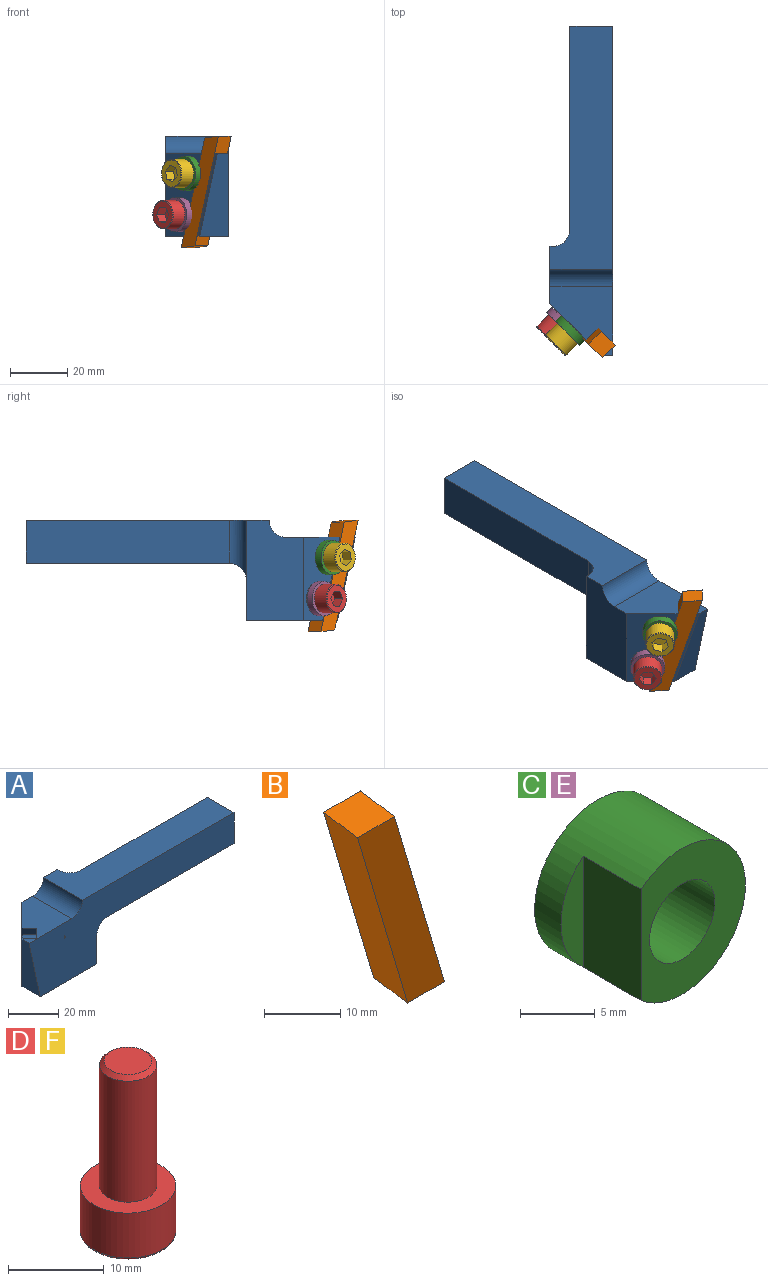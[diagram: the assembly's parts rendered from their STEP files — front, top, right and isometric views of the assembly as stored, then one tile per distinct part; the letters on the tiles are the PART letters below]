
ASSEMBLY  parts=6 mates=9
PART A: 26 faces, bbox 115x22.1x35 mm
  f0: plane 15x15mm, normal (1,0,0), area 225mm2, adj f4,f10,f22,f23
  f1: plane 4.64x4.64mm, normal (-0.68,-0.68,-0.29), area 13.6mm2, adj f7,f8,f15,f18
  f2: plane 5.8x5.4mm, normal (-0.68,-0.68,-0.29), area 35.7mm2, adj f8,f15,f17,f18
  f3: cylinder r=2.5mm len=11.38mm, axis (-0.71,0.71,0), area 174.3mm2, adj f4,f15,f16
  f4: plane 115.03x35.03mm, normal (0,-1,0), area 2230.9mm2, adj f0,f3,f6,f7,f10,f11,f12,f16
  f5: plane 29x6.77mm, normal (-0.71,0.71,0), area 25mm2, adj f6,f7,f12,f13
  f6: plane 24x22mm, normal (0,0,1), area 326.9mm2, adj f4,f5,f8,f9,f11,f12,f13,f14
  f7: plane 31.84x22mm, normal (0,0,-1), area 591.2mm2, adj f1,f4,f5,f8,f9,f12,f13,f15
  f8: plane 29x12.7mm, normal (-0.71,0.71,0), area 193.1mm2, adj f1,f2,f6,f7,f9,f14,f17,f18
  f9: plane 35x20mm, normal (0,1,0), area 635.7mm2, adj f6,f7,f8,f10,f11,f21
  f10: plane 85x22mm, normal (0,0,1), area 1338.7mm2, adj f0,f4,f9,f11,f21,f22,f24
  f11: cylinder r=6mm len=22mm, axis (0,1,0), area 207.3mm2, adj f4,f6,f9,f10
  f12: plane 29x10.16mm, normal (-0.98,0,-0.21), area 210mm2, adj f4,f5,f6,f7
  f13: plane 29x10.34mm, normal (0.68,0.68,0.29), area 178.7mm2, adj f5,f6,f7,f15
  f14: plane 4.99x4.99mm, normal (-0.68,-0.68,-0.29), area 23.8mm2, adj f6,f8,f15,f17
  f15: plane 29x16.43mm, normal (-0.71,0.71,0), area 354.4mm2, adj f1,f2,f3,f6,f7,f13,f14,f17
  f16: cone r=0mm half-angle=59deg, axis (-0.71,0.71,0), area 22.7mm2, adj f3,f4
  f17: cylinder r=6mm len=12.03mm, axis (-0.71,0.71,0), area 162.9mm2, adj f2,f8,f14,f15
  f18: cylinder r=6mm len=12.03mm, axis (-0.71,0.71,0), area 162.9mm2, adj f1,f2,f8,f15
  f19: cone r=0mm half-angle=59deg, axis (-0.71,0.71,0), area 22.9mm2, adj f20
  f20: cylinder r=2.5mm len=11.38mm, axis (-0.71,0.71,0), area 174.4mm2, adj f15,f19
  f21: plane 35x22mm, normal (1,0,0), area 329mm2, adj f4,f7,f9,f10,f24,f25
  f22: plane 71x15mm, normal (0,1,0), area 1065mm2, adj f0,f10,f23,f24
  f23: plane 71x15mm, normal (0,0,-1), area 1065mm2, adj f0,f4,f22,f25
  f24: cylinder r=6mm len=21mm, axis (0,0,1), area 161.9mm2, adj f10,f21,f22,f25
  f25: cylinder r=6mm len=21mm, axis (0,1,0), area 161.9mm2, adj f4,f21,f23,f24
PART B: 6 faces, bbox 21.7x11.8x37.7 mm
  f0: plane 37.68x14.84mm, normal (0.93,-0.06,0.37), area 254mm2, adj f1,f3,f4,f5
  f1: plane 6.84x6.28mm, normal (0,-0.15,0.99), area 43.4mm2, adj f0,f2,f4,f5
  f2: plane 37.68x14.84mm, normal (-0.93,0.06,-0.37), area 254mm2, adj f1,f3,f4,f5
  f3: plane 6.84x6.28mm, normal (0,0.15,-0.99), area 43.4mm2, adj f0,f2,f4,f5
  f4: plane 36.73x21.68mm, normal (0,-0.99,-0.15), area 254mm2, adj f0,f1,f2,f3
  f5: plane 36.73x21.68mm, normal (0,0.99,0.15), area 254mm2, adj f0,f1,f2,f3
PART C: 6 faces, bbox 12x8x12 mm
  f0: plane 12x9.9mm, normal (0,-1,0), area 69.6mm2, adj f1,f2,f4
  f1: cylinder r=3.1mm len=8mm, axis (0,1,0), area 155.8mm2, adj f0,f3
  f2: cylinder r=6mm len=12mm, axis (0,1,0), area 244.6mm2, adj f0,f3,f4,f5
  f3: plane 12x12mm, normal (0,1,0), area 82.9mm2, adj f1,f2
  f4: plane 9.12x5.5mm, normal (-1,0,0), area 50.2mm2, adj f0,f2,f5
  f5: plane 9.12x2.1mm, normal (0,-1,0), area 13.3mm2, adj f2,f4
PART D: 14 faces, bbox 10.8x10.8x22 mm
  f0: plane 10x10mm, normal (0,0,1), area 50.3mm2, adj f1,f3
  f1: cylinder r=5mm len=10mm, axis (0,0,-1), area 180.6mm2, adj f0,f12
  f2: plane 9.5x9.5mm, normal (0,0,-1), area 47.5mm2, adj f5,f6,f7,f8,f9,f10,f12
  f3: cylinder r=3mm len=15.5mm, axis (0,0,-1), area 292.2mm2, adj f0,f13
  f4: plane 5x5mm, normal (0,0,1), area 19.6mm2, adj f13
  f5: plane 4x2.6mm, normal (0.87,-0.5,0), area 12mm2, adj f2,f6,f10,f11
  f6: plane 4x2.6mm, normal (0.87,0.5,0), area 12mm2, adj f2,f5,f7,f11
  f7: plane 4x3mm, normal (0,1,0), area 12mm2, adj f2,f6,f8,f11
  f8: plane 4x2.6mm, normal (-0.87,0.5,0), area 12mm2, adj f2,f7,f9,f11
  f9: plane 4x2.6mm, normal (-0.87,-0.5,0), area 12mm2, adj f2,f8,f10,f11
  f10: plane 4x3mm, normal (0,-1,0), area 12mm2, adj f2,f5,f9,f11
  f11: plane 6x5.2mm, normal (0,0,-1), area 23.4mm2, adj f5,f6,f7,f8,f9,f10
  f12: torus R=4.75mm, axis (0,0,1), area 12.1mm2, adj f1,f2
  f13: cone r=2.5mm half-angle=45deg, axis (0,0,-1), area 12.2mm2, adj f3,f4
PART E: same geometry as C
PART F: same geometry as D
PLACE A rot(axis=(0,0,1),90deg) t=(-25,0,0)mm fixed
PLACE B rot(axis=(0.92,-0.39,0.01),170.1deg) t=(13.24,-125.88,-2.81)mm
PLACE C rot(axis=(0.15,-0.06,0.99),135.5deg) t=(-58.04,-65.13,-10.84)mm
PLACE D rot(axis=(0.29,0.67,0.68),149.9deg) t=(-64.36,-93.26,-15.39)mm
PLACE E rot(axis=(-0.92,0.38,0.02),179.3deg) t=(22.32,-145.5,-14.19)mm
PLACE F rot(axis=(-0.83,0.5,-0.24),93.4deg) t=(-7.89,-149.73,-34.79)mm
MATE cylindrical A.f3 <-> C.f1  axis (-0.71,-0.71,0) through (-13.74,-105.26,-13)mm
MATE planar C.f5 <-> B.f5  axis (0.71,0.71,0) through (-10.84,-108.8,-14.37)mm
MATE fastened E.f1 <-> D.f1  axis (-0.71,-0.71,0) through (-18.88,-104.29,-27.37)mm
MATE cylindrical E.f1 <-> A.f19  axis (-0.71,-0.71,0) through (-18.88,-104.29,-27.37)mm
MATE fastened C.f1 <-> F.f1  axis (-0.71,-0.71,0) through (-15.83,-107.35,-13)mm
MATE planar E.f5 <-> B.f5  axis (0.71,0.71,0) through (-20.47,-99.17,-27.21)mm
MATE planar B.f0 <-> A.f13  axis (0.68,-0.68,-0.29) through (-5.48,-109.67,-19.15)mm
MATE parallel C.f4 <-> B.f2  axis (0.68,-0.68,-0.29) through (-9.47,-106.28,-14.12)mm
MATE planar B.f4 <-> A.f15  axis (0.71,0.71,0) through (-5.64,-105.01,-19.45)mm
